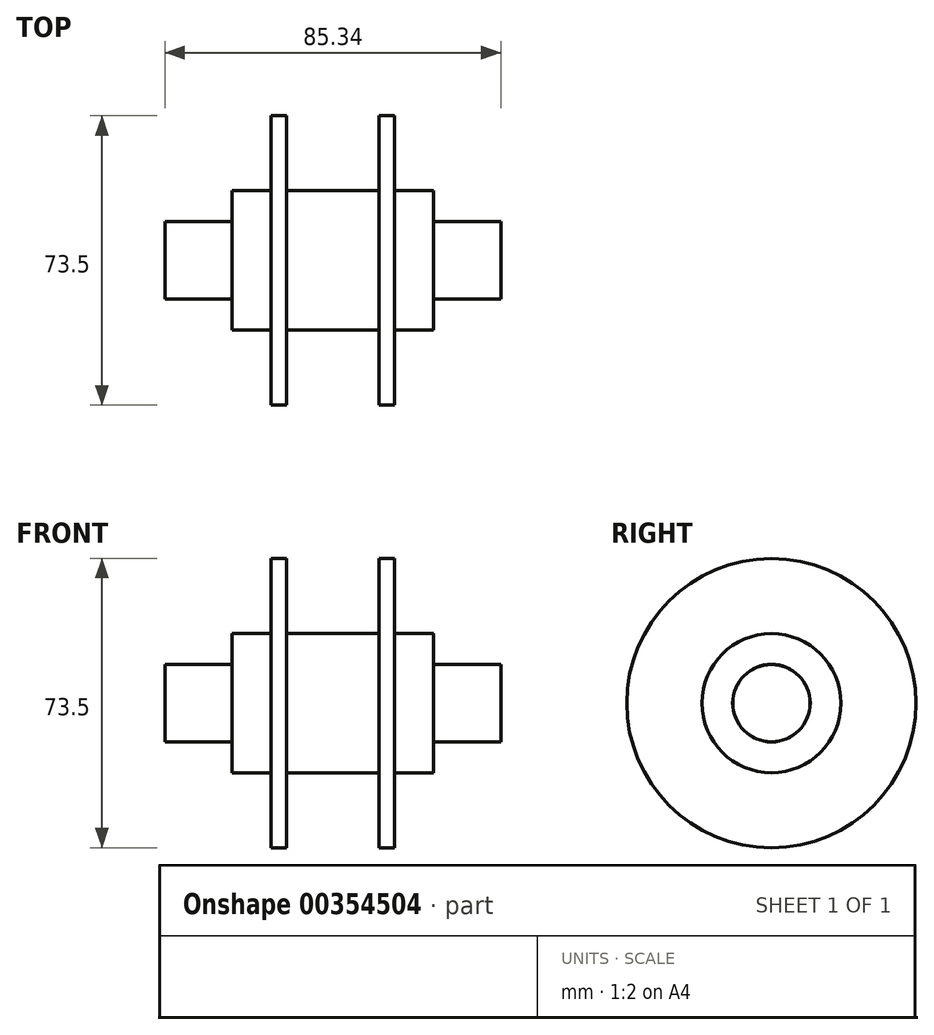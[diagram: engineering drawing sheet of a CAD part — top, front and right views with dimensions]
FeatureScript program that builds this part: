
annotation { "Feature Type Name" : "Feature", "Feature Type Description" : "" }
export const myFeature = defineFeature(function(context is Context, id is Id, definition is map)
    precondition{}
    {
        {
            var Q0;
            Q0=qCreatedBy(makeId("Front.planeOp"),FACE);
            var sketch = newSketch(context, id + "F0", { "sketchPlane" : qUnion([Q0])});
            skLineSegment(sketch, "E0", {"start": v(0, 0) * mm, "end": v(-42.67, 0) * mm});
            skLineSegment(sketch, "E1", {"start": v(-42.67, 0) * mm, "end": v(-42.67, 9.8) * mm});
            skLineSegment(sketch, "E2", {"start": v(0, 0) * mm, "end": v(0, 17.67) * mm});
            skLineSegment(sketch, "E3", {"start": v(0, 17.67) * mm, "end": v(-11.73, 17.67) * mm});
            skLineSegment(sketch, "E4", {"start": v(-11.73, 17.67) * mm, "end": v(-11.73, 36.75) * mm});
            skLineSegment(sketch, "E5", {"start": v(-11.73, 36.75) * mm, "end": v(-15.65, 36.75) * mm});
            skLineSegment(sketch, "E6", {"start": v(-15.65, 36.75) * mm, "end": v(-15.65, 17.67) * mm});
            skLineSegment(sketch, "E7", {"start": v(-15.65, 17.67) * mm, "end": v(-25.63, 17.67) * mm});
            skLineSegment(sketch, "E8", {"start": v(-25.63, 17.67) * mm, "end": v(-25.63, 9.85) * mm});
            skLineSegment(sketch, "E9", {"start": v(-25.63, 9.85) * mm, "end": v(-42.67, 9.8) * mm});
            skSolve(sketch);
        }
        {
            var Q0;
            Q0=makeQuery(id+"F0.imprint","IMPRINT",FACE,{"disambiguationData":[TD([[makeQuery(id+"F0.imprint","IMPRINT",EDGE,{"derivedFrom":sQuery(id+"F0.wireOp",EDGE,"E0")}),-1.0]])]});
            var Q1;
            Q1=sQuery(id+"F0.wireOp",EDGE,"E0");
            revolve(context, id + "F1", {"entities" : qUnion([Q0]), "axis" : qUnion([Q1]), "revolveType" : RevolveType.FULL});
        }
        {
            var Q0;
            Q0=makeQuery(id+"F1.opRevolve","SWEPT_BODY",BODY,{"disambiguationData":[OSD([sQuery(id+"F0.wireOp",EDGE,"E0"),sQuery(id+"F0.wireOp",EDGE,"E1"),sQuery(id+"F0.wireOp",EDGE,"E2"),sQuery(id+"F0.wireOp",EDGE,"E3"),sQuery(id+"F0.wireOp",EDGE,"E4"),sQuery(id+"F0.wireOp",EDGE,"E5"),sQuery(id+"F0.wireOp",EDGE,"E6"),sQuery(id+"F0.wireOp",EDGE,"E7"),sQuery(id+"F0.wireOp",EDGE,"E8"),sQuery(id+"F0.wireOp",EDGE,"E9")])]});
            var Q1;
            Q1=qCreatedBy(makeId("Right.planeOp"),FACE);
            mirror(context, id + "F2", {"operationType" : NewBodyOperationType.ADD, "entities" : qUnion([Q0]), "mirrorPlane" : qUnion([Q1])});
        }
    });
